# Revit family: 0974218333
name_source: partatom
category: Plumbing Fixtures
revit_build: Autodesk Revit 2018 (Build: 20170223_1515(x64)
units: mm (PartAtom-declared; Revit-internal decimal feet)

## family parameters
Always vertical = Yes
Cut with Voids When Loaded = No
OmniClass Number = 23.45.55.00
OmniClass Title = Sanitary Faucets, Wastes
Part Type = Normal
Room Calculation Point = No
Round Connector Dimension = Use Diameter
Shared = No
Work Plane-Based = No

## types (1)
- 0974218333 Bath and shower faucet
    2D/3D/BIM Files URL = http://static.hansa.com
    Advanced Features = DZR brass
    Approval ABP = PA-IX 29490/IDB
    Approval ACS = 16 ACC NY 205
    Approval CSTB = 322-M1-20/1
    Approval KIWA = K6116/08
    AssetType = Fixed
    BIMObjectName = 0974218333
    BodyMaterial = Brass
    Brand = Hansa
    Category = Bathroom
    Class = Single lever
    CloseOffRating = 0
    Color = Black Matt
    Connection = Eccentric unions;
    Connection Size = G1/2
    Customs Code = 84818011
    DN Size = DN15
    Dimension Drawing URL = http://static.hansa.com
    Diverter = Pull diverter;Integrated diverter / automatic reset
    DurationUnit = Year
    EAN Number = 4057304014345
    EN Standard = EN 817
    FDV Document URL = http://www.hansa.com
    FaucetMainMaterial = Brass
    Features = Single lever
    Finish = Polished
    Flow Drawing URL = http://static.hansa.com
    Flow Rate At 300kPa = 0.3 L/s
    FlowCoefficient = 0
    Group = Bath and shower faucets
    IfcExportAs = IfcValveType
    IfcExportType = FAUCET
    Installation Type = Wall mounted
    Installation and Maintenance = http://static.hansa.com
    Lever Handle = Lever with H+C symbol;
    Manufacturer = Hansa
    ManufacturerName = Hansa
    ManufacturerURL = http://www.hansa.com
    Market = INT;DEU;AUT;BEL;NLD;FRA;CZE;SVK;ITA;ESP
    Material = Brass
    Max. Hot Water Supply = 90 °C
    Mechanical Parts = Non-return valve(s);
    Model = 0974218333 Bath and shower faucet
    ModelReference = 0974218333
    NBSDescription = Water supply fittings for baths
    NBSReference = 45-35-70/315
    Name = 0974218333 Bath and shower faucet
    Name_en = 0974218333 Bath and shower faucet
    Noise Class = I (ISO 3822)
    NominalDepth = 179 mm
    NominalHeight = 120 mm
    NominalWidth = 215 mm
    Package Weight = 2.38 kg
    Package external Dimensions = 210 x 176 x 162
    Pressure Loss With Flow 03ls = 250000.0 Pa
    Product Code = 0974218333
    Product Datasheet = http://www.hansa.com
    Product Family = HANSATWIST
    Product Image URL = http://static.hansa.com
    Product URL = http://static.hansa.com
    Projection = 162 mm
    Shape = Sculptured
    Size = 215x180x120 mm
    Spare Parts = http://static.hansa.com
    Spout Type = Fixed spout
    Technical DataSheet URL = http://www.hansa.com
    Temperature Adjustments = Temperature limiter;Temperature limiter (retrofittable)
    URL ABP = http://static.hansa.com
    Uniclass2 = Pr_40_30_96_81
    Uniclass2015Description = Shower thermostatic water supply sets
    Uniclass2015Reference = Pr_40_20_87_81
    Version = 1
    VersionDate = 15/02/2021
    WarrantyDescription = http://warranty.hansa.com
    WarrantyDurationUnit = Year
    WorkingPressure = 100 - 1000 kPa

## geometry (parser evidence)
native form markers: Sweep x5
no freeform markers — native parametric forms only
